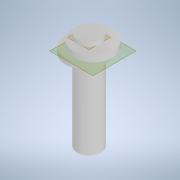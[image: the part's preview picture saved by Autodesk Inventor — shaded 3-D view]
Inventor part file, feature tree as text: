
AUTODESK INVENTOR PART (.ipt)
format: ipt  version: 2022 (Build 260153000, 153)  size: 149,504 bytes
history: native  units: in
note: dims shown in document units (in); Inventor stores cm internally (conversion verified against a paired STEP export)
features: sketch x5, extrude x4, plane x2, fillet x1
ambient origin geometry x8: Origin, YZ Plane, XZ Plane, XY Plane, X Axis, Y Axis, Z Axis, Center Point
bodies: Solid1 (feature_tree)
feature tree (12):
  sketch  "Sketch1"  dims[d1=1.9685in d2=0.0in d3=-0.0787in]
  extrude  "Extrusion1"  [1 undecoded]
  plane  "Work Plane1"
  extrude  "Extrusion2"  Depth=0.7874in
  plane  "Work Plane2"
  extrude  "Extrusion4"  Depth=0.0787in
  extrude  "Extrusion5"  Depth=0.7874in
  fillet  "Fillet1"  Radius=0.1181in
  sketch  "Sketch2"  dims[d4=0.0787in d5=0.7874in]
  sketch  "Sketch3"  dims[d6=0.1181in d7=0.0in d8=0.0787in]
  sketch  "Sketch5"  dims[d16=0.0787in d17=0.7874in d18=0.1181in d19=0.0in]
  sketch  "Sketch6"  dims[d20=0.4724in d21=0.1575in d22=0.0in d23=0.0394in]
note: 1 required parameter value undecoded (feature->parameter linkage not recoverable at this tier; creation-order binding heuristic only, values carry confidence <= 0.55)
